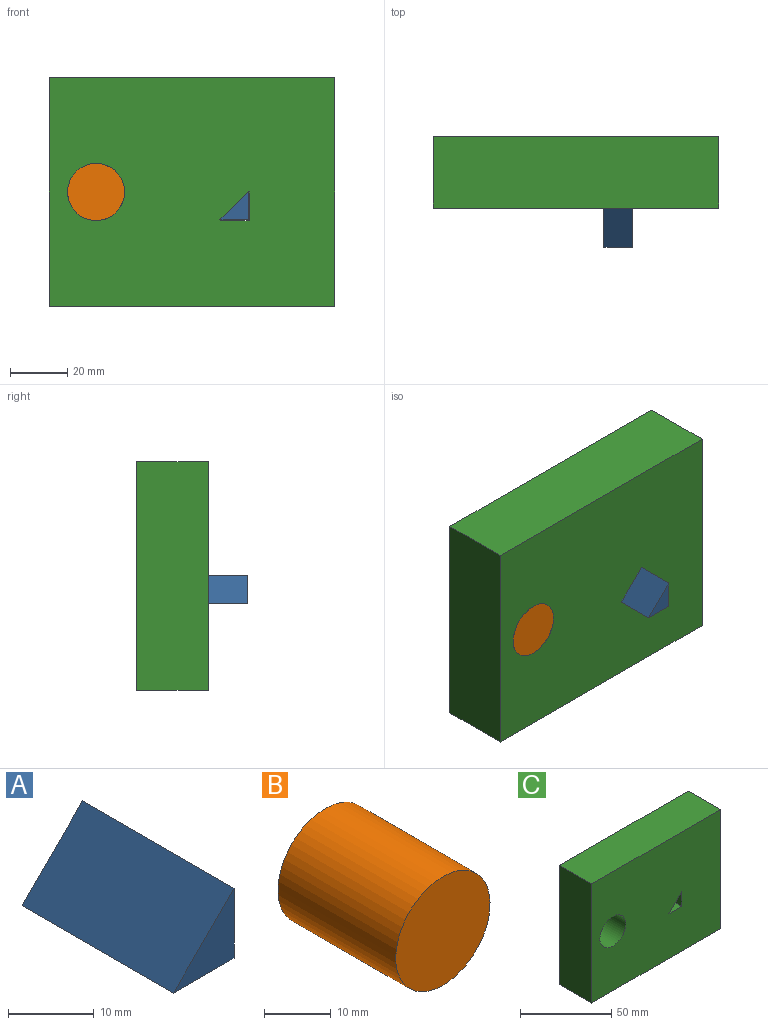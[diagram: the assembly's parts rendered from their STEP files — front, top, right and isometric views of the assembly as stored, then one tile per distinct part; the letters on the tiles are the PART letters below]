
ASSEMBLY  parts=3 mates=2
PART A: 5 faces, bbox 10x25x10 mm
  f0: plane 25x10mm, normal (-0.71,0,0.71), area 353.6mm2, adj f1,f2,f3,f4
  f1: plane 25x10mm, normal (0,0,-1), area 250mm2, adj f0,f2,f3,f4
  f2: plane 25x10mm, normal (1,0,0), area 250mm2, adj f0,f1,f3,f4
  f3: plane 10x10mm, normal (0,-1,0), area 50mm2, adj f0,f1,f2
  f4: plane 10x10mm, normal (0,1,0), area 50mm2, adj f0,f1,f2
PART B: 3 faces, bbox 20x25x20 mm
  f0: cylinder r=10mm len=25mm, axis (0,1,0), area 1570.8mm2, adj f1,f2
  f1: plane 20x20mm, normal (0,-1,0), area 314.2mm2, adj f0
  f2: plane 20x20mm, normal (0,1,0), area 314.2mm2, adj f0
PART C: 10 faces, bbox 100x25x80 mm
  f0: plane 100x80mm, normal (0,-1,0), area 7635.8mm2, adj f2,f3,f4,f5,f6,f7,f8,f9
  f1: plane 100x80mm, normal (0,1,0), area 7635.8mm2, adj f2,f3,f4,f5,f6,f7,f8,f9
  f2: plane 100x25mm, normal (0,0,1), area 2500mm2, adj f0,f1,f3,f5
  f3: plane 80x25mm, normal (-1,0,0), area 2000mm2, adj f0,f1,f2,f4
  f4: plane 100x25mm, normal (0,0,-1), area 2500mm2, adj f0,f1,f3,f5
  f5: plane 80x25mm, normal (1,0,0), area 2000mm2, adj f0,f1,f2,f4
  f6: cylinder r=10mm len=25mm, axis (0,-1,0), area 1570.8mm2, adj f0,f1
  f7: plane 25x10mm, normal (0.71,0,-0.71), area 353.6mm2, adj f0,f1,f8,f9
  f8: plane 25x10mm, normal (0,0,1), area 250mm2, adj f0,f1,f7,f9
  f9: plane 25x10mm, normal (-1,0,0), area 250mm2, adj f0,f1,f7,f8
PLACE A t=(-21.82,-46.46,-18.23)mm
PLACE B rot(axis=(0,1,0),35.6deg) t=(-67.98,-32.78,-9.04)mm
PLACE C t=(-34.36,-32.78,-9.04)mm fixed
MATE slider C.f0 <-> A.f3  axis (0,-1,0) through (-17.9,-57.78,-15.5)mm
MATE revolute C.f6 <-> B.f0  axis (0,-1,0) through (-67.98,-57.78,-9.04)mm
